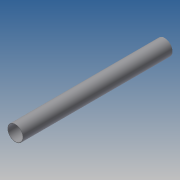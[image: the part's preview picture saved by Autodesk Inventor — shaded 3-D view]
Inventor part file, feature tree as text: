
AUTODESK INVENTOR PART (.ipt)
format: ipt  version: 2014 SP1 (Build 180222100, 222)  size: 124,416 bytes
history: native  units: in
note: dims shown in document units (in); Inventor stores cm internally (conversion verified against a paired STEP export)
features: extrude x1, sketch x1
ambient origin geometry x8: Origin, YZ Plane, XZ Plane, XY Plane, X Axis, Y Axis, Z Axis, Center Point
bodies: Solid1 (feature_tree)
feature tree (2):
  extrude  "Extrusion1"  Depth=59.0551in
  sketch  "Sketch1"  dims[d0=5.8in d1=0.2in d2=59.0551in d3=0.0in]
